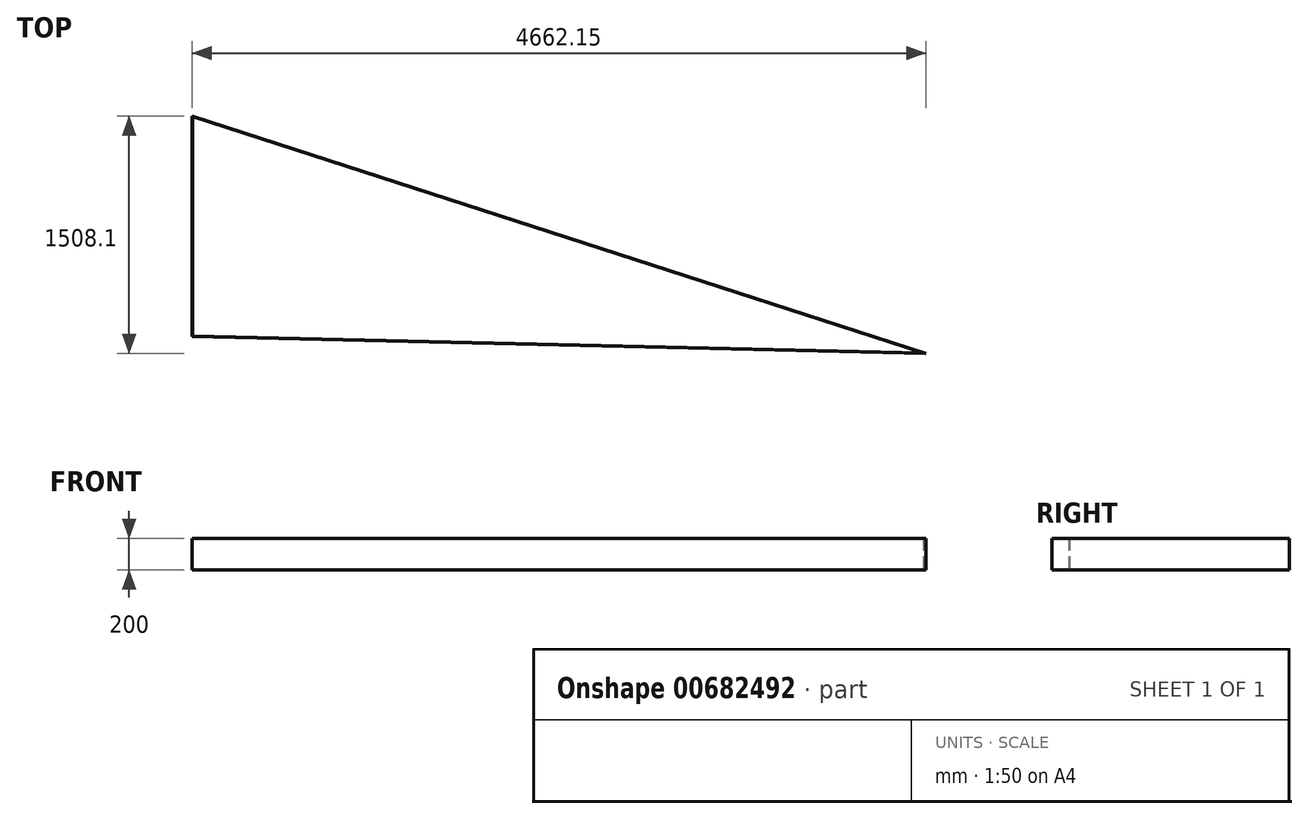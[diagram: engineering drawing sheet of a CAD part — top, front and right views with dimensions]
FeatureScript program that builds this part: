
annotation { "Feature Type Name" : "Feature", "Feature Type Description" : "" }
export const myFeature = defineFeature(function(context is Context, id is Id, definition is map)
    precondition{}
    {
        {
            var Q0;
            Q0=qCreatedBy(makeId("Top.planeOp"),FACE);
            var sketch = newSketch(context, id + "F0", { "sketchPlane" : qUnion([Q0])});
            skLineSegment(sketch, "E0", {"start": v(-2320.38, 1845.58) * mm, "end": v(2341.77, 337.48) * mm});
            skLineSegment(sketch, "E1", {"start": v(-2320.38, 1845.58) * mm, "end": v(-2320.38, 445.58) * mm});
            skLineSegment(sketch, "E2", {"start": v(-2320.38, 445.58) * mm, "end": v(2341.77, 337.48) * mm});
            skSolve(sketch);
        }
        {
            var Q0;
            Q0=makeQuery(id+"F0.imprint","IMPRINT",FACE,{"disambiguationData":[TD([[makeQuery(id+"F0.imprint","IMPRINT",EDGE,{"derivedFrom":sQuery(id+"F0.wireOp",EDGE,"E0")}),-1.0]])]});
            extrude(context, id + "F1", {"entities" : qUnion([Q0]), "depth" : 200 * mm, "offsetDistance" : 25.4 * mm});
        }
        {
            var Q0;
            Q0=makeQuery(id+"F1.opExtrude","CAP_FACE",FACE,{"disambiguationData":[OSD([sQuery(id+"F0.wireOp",EDGE,"E0"),sQuery(id+"F0.wireOp",EDGE,"E1"),sQuery(id+"F0.wireOp",EDGE,"E2")])],"isStart":false});
            shell(context, id + "F2", {"entities" : qUnion([Q0]), "thickness" : 2.54 * mm});
        }
    });
